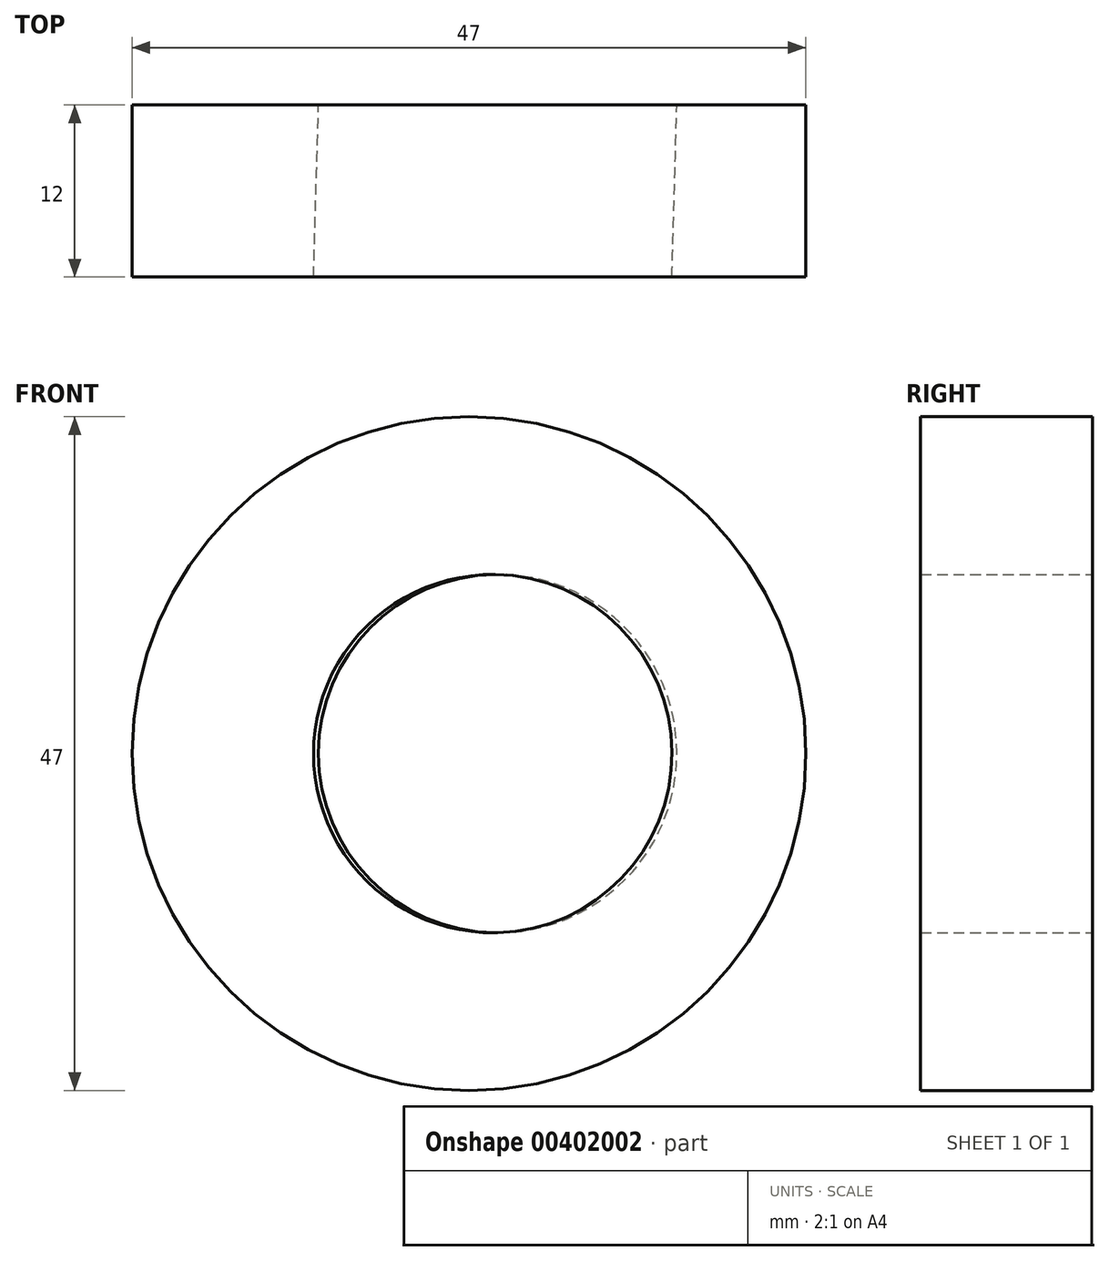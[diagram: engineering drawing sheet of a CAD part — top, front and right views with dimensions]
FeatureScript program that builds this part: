
annotation { "Feature Type Name" : "Feature", "Feature Type Description" : "" }
export const myFeature = defineFeature(function(context is Context, id is Id, definition is map)
    precondition{}
    {
        {
            var Q0;
            Q0=qCreatedBy(makeId("Front.planeOp"),FACE);
            var sketch = newSketch(context, id + "F0", { "sketchPlane" : qUnion([Q0])});
            skCircle(sketch, "E0", {"center": v(0, 0) * mm, "radius": 23.5 * mm});
            skCircle(sketch, "E1", {"center": v(2, 0) * mm, "radius": 12.5 * mm});
            skSolve(sketch);
        }
        {
            var Q0;
            Q0=qCreatedBy(makeId("Top.planeOp"),FACE);
            var sketch = newSketch(context, id + "F1", { "sketchPlane" : qUnion([Q0])});
            skPoint(sketch, "E2.0", {"position": v(2, 0) * mm});
            skLineSegment(sketch, "E3", {"start": v(2, 0) * mm, "end": v(1.65, -13.32) * mm, "construction": true});
            skSolve(sketch);
        }
        {
            var Q0;
            Q0=qCreatedBy(makeId("Front.planeOp"),FACE);
            cPlane(context, id + "F2", {"entities" : qUnion([Q0]), "cplaneType" : CPlaneType.OFFSET, "offset" : 12 * mm, "width" : 150 * mm, "height" : 150 * mm});
        }
        {
            var Q0;
            Q0=qCreatedBy(id+"F2.planeOp",FACE);
            var sketch = newSketch(context, id + "F3", { "sketchPlane" : qUnion([Q0])});
            skCircle(sketch, "E4.0", {"center": v(0, 0) * mm, "radius": 23.5 * mm});
            skCircle(sketch, "E5", {"center": v(1.65, 0) * mm, "radius": 12.5 * mm});
            skLineSegment(sketch, "E6.0", {"start": v(2, 0) * mm, "end": v(1.65, 0) * mm, "construction": true});
            skSolve(sketch);
        }
        {
            var Q0;
            Q0=makeQuery(id+"F0.imprint","IMPRINT",FACE,{"disambiguationData":[TD([[makeQuery(id+"F0.imprint","IMPRINT",EDGE,{"derivedFrom":sQuery(id+"F0.wireOp",EDGE,"E0")}),1.0]])]});
            var Q1;
            Q1=makeQuery(id+"F0.imprint","IMPRINT",FACE,{"disambiguationData":[TD([[makeQuery(id+"F0.imprint","IMPRINT",EDGE,{"derivedFrom":sQuery(id+"F0.wireOp",EDGE,"E1")}),1.0]])]});
            var Q2;
            Q2=sQuery(id+"F0.wireOp",EDGE,"E0");
            var Q3;
            Q3=qCreatedBy(id+"F2.planeOp",FACE);
            extrude(context, id + "F4", {"entities" : qUnion([Q0, Q1]), "surfaceEntities" : qUnion([Q2]), "endBound" : BoundingType.UP_TO_SURFACE, "endBoundEntityFace" : qUnion([Q3]), "depth" : 25 * mm});
        }
        {
            var Q1;
            Q1=makeQuery(id+"F0.imprint","IMPRINT",FACE,{"disambiguationData":[TD([[makeQuery(id+"F0.imprint","IMPRINT",EDGE,{"derivedFrom":sQuery(id+"F0.wireOp",EDGE,"E1")}),1.0]])]});
            var Q2;
            Q2=makeQuery(id+"F3.imprint","IMPRINT",FACE,{"disambiguationData":[TD([[makeQuery(id+"F3.imprint","IMPRINT",EDGE,{"derivedFrom":sQuery(id+"F3.wireOp",EDGE,"E5")}),1.0]])]});
            loft(context, id + "F5", {"operationType" : NewBodyOperationType.REMOVE, "sheetProfilesArray" : [{ "sheetProfileEntities" : qUnion([Q1]) }, { "sheetProfileEntities" : qUnion([Q2]) }]});
        }
    });
